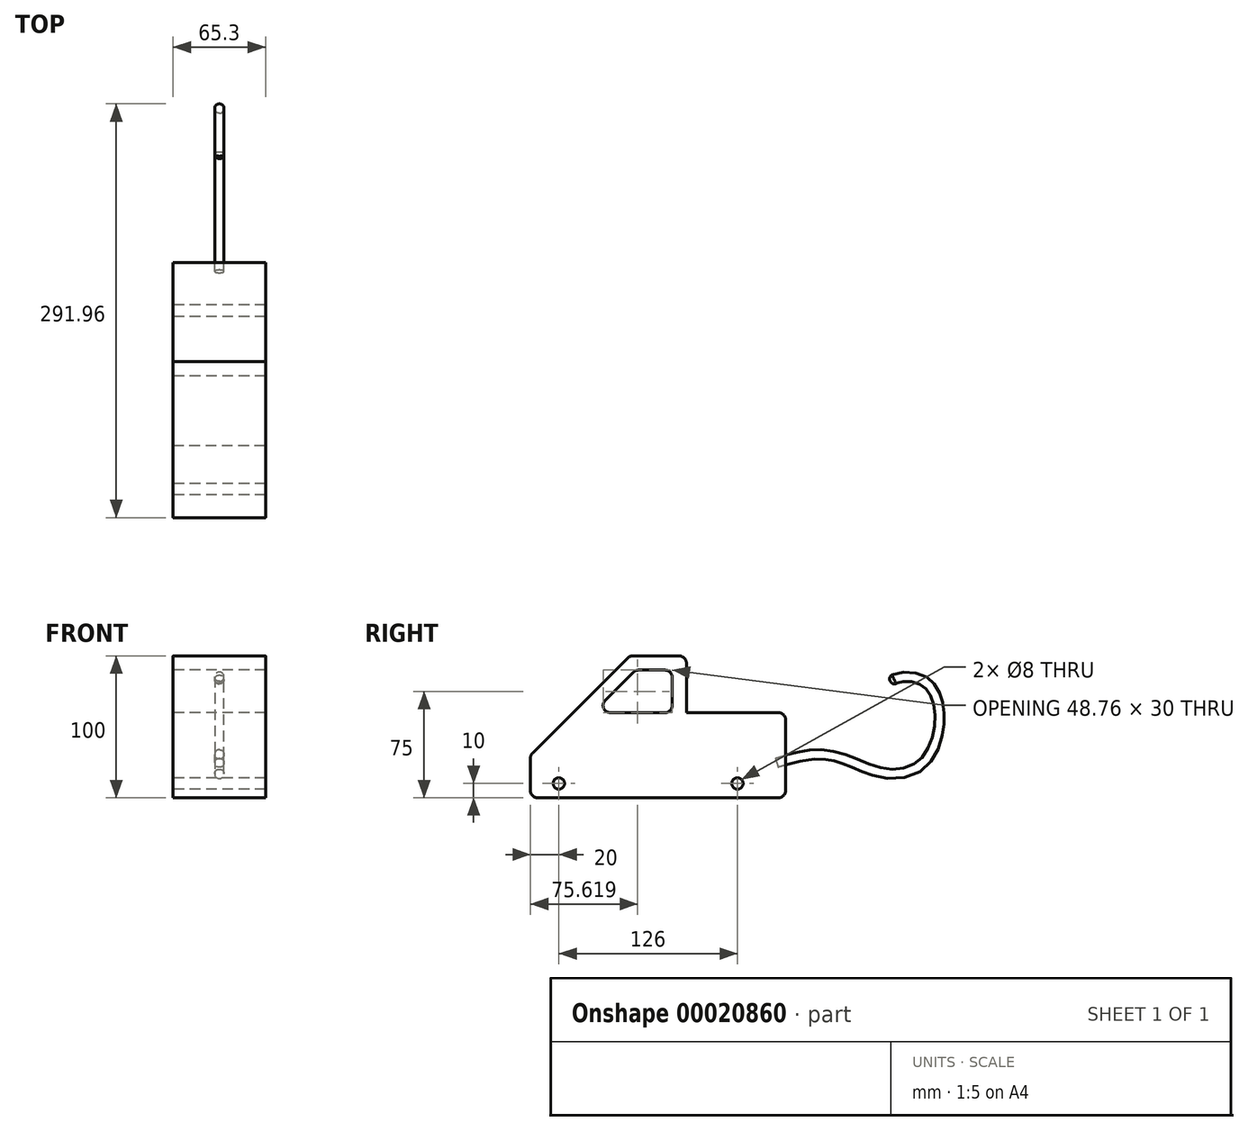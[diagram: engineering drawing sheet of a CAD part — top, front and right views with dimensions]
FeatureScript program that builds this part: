
annotation { "Feature Type Name" : "Feature", "Feature Type Description" : "" }
export const myFeature = defineFeature(function(context is Context, id is Id, definition is map)
    precondition{}
    {
        {
            var Q0;
            Q0=qCreatedBy(makeId("Right.planeOp"),FACE);
            var sketch = newSketch(context, id + "F0", { "sketchPlane" : qUnion([Q0])});
            skLineSegment(sketch, "E0", {"start": v(0, 0) * mm, "end": v(0, 30) * mm});
            skLineSegment(sketch, "E1", {"start": v(0, 30) * mm, "end": v(70, 100) * mm});
            skLineSegment(sketch, "E2", {"start": v(70, 100) * mm, "end": v(110, 100) * mm});
            skLineSegment(sketch, "E3", {"start": v(110, 100) * mm, "end": v(110, 60) * mm});
            skLineSegment(sketch, "E4", {"start": v(110, 60) * mm, "end": v(180, 60) * mm});
            skLineSegment(sketch, "E5", {"start": v(180, 60) * mm, "end": v(180, 0) * mm});
            skLineSegment(sketch, "E6", {"start": v(180, 0) * mm, "end": v(0, 0) * mm});
            skLineSegment(sketch, "E7.0", {"start": v(100, 90) * mm, "end": v(100, 60) * mm});
            skLineSegment(sketch, "E7.1", {"start": v(74.14, 90) * mm, "end": v(100, 90) * mm});
            skLineSegment(sketch, "E7.2", {"start": v(44.14, 60) * mm, "end": v(74.14, 90) * mm});
            skLineSegment(sketch, "E8", {"start": v(100, 60) * mm, "end": v(44.14, 60) * mm});
            skCircle(sketch, "E9", {"center": v(20, 10) * mm, "radius": 4 * mm});
            skCircle(sketch, "E10", {"center": v(146, 10) * mm, "radius": 4 * mm});
            skSolve(sketch);
        }
        {
            var Q0;
            Q0=makeQuery(id+"F0.imprint","IMPRINT",FACE,{"disambiguationData":[TD([[makeQuery(id+"F0.imprint","IMPRINT",EDGE,{"derivedFrom":sQuery(id+"F0.wireOp",EDGE,"E0")}),-1.0]])]});
            extrude(context, id + "F1", {"entities" : qUnion([Q0]), "endBound" : BoundingType.SYMMETRIC, "depth" : 65.3 * mm});
        }
        {
            var Q0;
            Q0=makeQuery(id+"F1.opExtrude","SWEPT_EDGE",EDGE,{"disambiguationData":[OSD([sQuery(id+"F0.wireOp",EDGE,"E0"),sQuery(id+"F0.wireOp",EDGE,"E6")])]});
            var Q1;
            Q1=makeQuery(id+"F1.opExtrude","SWEPT_EDGE",EDGE,{"disambiguationData":[OSD([sQuery(id+"F0.wireOp",EDGE,"E0"),sQuery(id+"F0.wireOp",EDGE,"E1")])]});
            var Q2;
            Q2=makeQuery(id+"F1.opExtrude","SWEPT_EDGE",EDGE,{"disambiguationData":[OSD([sQuery(id+"F0.wireOp",EDGE,"E1"),sQuery(id+"F0.wireOp",EDGE,"E2")])]});
            var Q3;
            Q3=makeQuery(id+"F1.opExtrude","SWEPT_EDGE",EDGE,{"disambiguationData":[OSD([sQuery(id+"F0.wireOp",EDGE,"E2"),sQuery(id+"F0.wireOp",EDGE,"E3")])]});
            var Q4;
            Q4=makeQuery(id+"F1.opExtrude","SWEPT_EDGE",EDGE,{"disambiguationData":[OSD([sQuery(id+"F0.wireOp",EDGE,"E4"),sQuery(id+"F0.wireOp",EDGE,"E5")])]});
            var Q5;
            Q5=makeQuery(id+"F1.opExtrude","SWEPT_EDGE",EDGE,{"disambiguationData":[OSD([sQuery(id+"F0.wireOp",EDGE,"E5"),sQuery(id+"F0.wireOp",EDGE,"E6")])]});
            var Q6;
            Q6=makeQuery(id+"F1.opExtrude","SWEPT_EDGE",EDGE,{"disambiguationData":[OSD([sQuery(id+"F0.wireOp",EDGE,"E7.0"),sQuery(id+"F0.wireOp",EDGE,"E8")])]});
            var Q7;
            Q7=makeQuery(id+"F1.opExtrude","SWEPT_EDGE",EDGE,{"disambiguationData":[OSD([sQuery(id+"F0.wireOp",EDGE,"E7.0"),sQuery(id+"F0.wireOp",EDGE,"E7.1")])]});
            var Q8;
            Q8=makeQuery(id+"F1.opExtrude","SWEPT_EDGE",EDGE,{"disambiguationData":[OSD([sQuery(id+"F0.wireOp",EDGE,"E7.1"),sQuery(id+"F0.wireOp",EDGE,"E7.2")])]});
            var Q9;
            Q9=makeQuery(id+"F1.opExtrude","SWEPT_EDGE",EDGE,{"disambiguationData":[OSD([sQuery(id+"F0.wireOp",EDGE,"E7.2"),sQuery(id+"F0.wireOp",EDGE,"E8")])]});
            fillet(context, id + "F2", {"entities" : qUnion([Q0, Q1, Q2, Q3, Q4, Q5, Q6, Q7, Q8, Q9]), "radius" : 5 * mm, "tangentPropagation" : true, "allowEdgeOverflow" : false});
        }
        {
            var Q0;
            Q0=qCreatedBy(makeId("Right.planeOp"),FACE);
            var sketch = newSketch(context, id + "F3", { "sketchPlane" : qUnion([Q0])});
            skFitSpline(sketch, "E11", {"points": [v(173.77, 24.63) * mm, v(197.88, 30.32) * mm, v(221.37, 27.31) * mm, v(248.27, 17.46) * mm, v(274.73, 22.47) * mm, v(287.49, 45.52) * mm, v(286.8, 69.41) * mm, v(276.95, 82.63) * mm, v(261.22, 85.03) * mm, v(253.81, 82.14) * mm], "startDerivative": vector(200.24, 61.88) * mm, "endDerivative": vector(-93.6, -51.86) * mm});
            skSolve(sketch);
        }
        {
            var Q0;
            Q0=sQuery(id+"F3.wireOp",EDGE,"E11");
            var Q1;
            Q1=sQuery(id+"F3.wireOp",VERTEX,"E11.start");
            cPlane(context, id + "F4", {"entities" : qUnion([Q0, Q1]), "cplaneType" : CPlaneType.CURVE_POINT, "offset" : 150 * mm, "width" : 150 * mm, "height" : 150 * mm});
        }
        {
            var Q0;
            Q0=qCreatedBy(id+"F4.planeOp",FACE);
            var sketch = newSketch(context, id + "F5", { "sketchPlane" : qUnion([Q0])});
            skCircle(sketch, "E12", {"center": v(0, -27.77) * mm, "radius": 3.32 * mm});
            skSolve(sketch);
        }
        {
            var Q0;
            Q0=makeQuery(id+"F5.imprint","IMPRINT",FACE,{"disambiguationData":[TD([[makeQuery(id+"F5.imprint","IMPRINT",EDGE,{"derivedFrom":sQuery(id+"F5.wireOp",EDGE,"E12")}),1.0]])]});
            var Q1;
            Q1=sQuery(id+"F3.wireOp",EDGE,"E11");
            sweep(context, id + "F6", {"profiles" : qUnion([Q0]), "path" : qUnion([Q1])});
        }
        {
            var Q0;
            Q0=makeQuery(id+"F6.opSweep","CAP_EDGE",EDGE,{"disambiguationData":[OSD([sQuery(id+"F3.wireOp",VERTEX,"E11.end"),sQuery(id+"F5.wireOp",EDGE,"E12")])],"isStart":false});
            fillet(context, id + "F7", {"entities" : qUnion([Q0]), "radius" : 3 * mm, "tangentPropagation" : true, "allowEdgeOverflow" : false});
        }
    });
